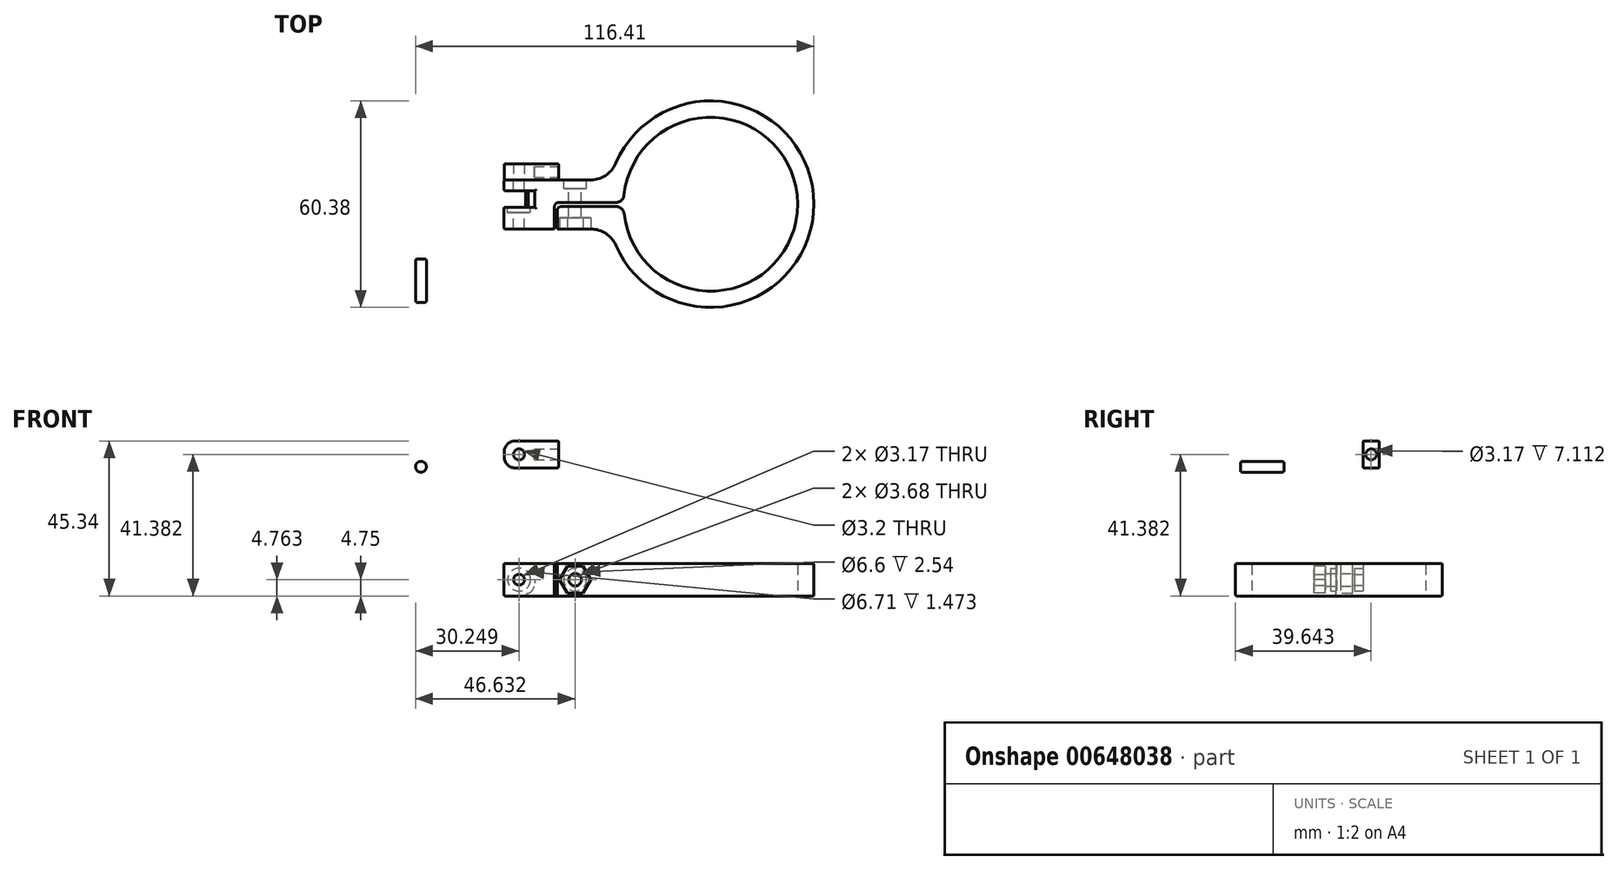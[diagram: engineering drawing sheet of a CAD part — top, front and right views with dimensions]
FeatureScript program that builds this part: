
annotation { "Feature Type Name" : "Feature", "Feature Type Description" : "" }
export const myFeature = defineFeature(function(context is Context, id is Id, definition is map)
    precondition{}
    {
        {
            var Q0;
            Q0=qCreatedBy(makeId("Top.planeOp"),FACE);
            var sketch = newSketch(context, id + "F0", { "sketchPlane" : qUnion([Q0])});
            skLineSegment(sketch, "E0", {"start": v(89.23, 15.92) * mm, "end": v(-89.23, 15.92) * mm, "construction": true});
            skLineSegment(sketch, "E1", {"start": v(-28, 19.91) * mm, "end": v(-19.37, 19.91) * mm});
            skLineSegment(sketch, "E2", {"start": v(-28, 15.1) * mm, "end": v(-19.37, 15.1) * mm});
            skLineSegment(sketch, "E3", {"start": v(-23.98, -123.91) * mm, "end": v(-23.98, 123.91) * mm, "construction": true});
            skLineSegment(sketch, "E4", {"start": v(-28.4, 20.3) * mm, "end": v(-28.4, 22.7) * mm});
            skLineSegment(sketch, "E5", {"start": v(-28.4, 14.7) * mm, "end": v(-28.4, 9.15) * mm});
            skLineSegment(sketch, "E6", {"start": v(-19.37, 15.1) * mm, "end": v(-19.37, 19.91) * mm});
            skArc(sketch, "E7", {"start": v(-28.4, 20.3) * mm, "mid": v(-28.28, 20.03) * mm, "end": v(-28, 19.91) * mm});
            skArc(sketch, "E8", {"start": v(-28, 15.1) * mm, "mid": v(-28.28, 14.98) * mm, "end": v(-28.4, 14.7) * mm});
            skLineSegment(sketch, "E9", {"start": v(-25.57, 13.58) * mm, "end": v(-25.57, 8.75) * mm, "construction": true});
            skLineSegment(sketch, "E10", {"start": v(-22.4, 13.58) * mm, "end": v(-22.4, 8.75) * mm, "construction": true});
            skLineSegment(sketch, "E11", {"start": v(-22.4, 19.91) * mm, "end": v(-22.4, 23.09) * mm, "construction": true});
            skLineSegment(sketch, "E12", {"start": v(-25.57, 19.91) * mm, "end": v(-25.57, 23.09) * mm, "construction": true});
            skLineSegment(sketch, "E13", {"start": v(-28, 23.09) * mm, "end": v(-3.05, 23.09) * mm});
            skLineSegment(sketch, "E14", {"start": v(-25.57, 15.13) * mm, "end": v(-25.57, 19.89) * mm, "construction": true});
            skLineSegment(sketch, "E15", {"start": v(-22.4, 15.13) * mm, "end": v(-22.4, 19.89) * mm, "construction": true});
            skLineSegment(sketch, "E16", {"start": v(-28, 8.75) * mm, "end": v(-14, 8.75) * mm});
            skArc(sketch, "E17", {"start": v(-28.4, 9.15) * mm, "mid": v(-28.28, 8.87) * mm, "end": v(-28, 8.75) * mm});
            skArc(sketch, "E18", {"start": v(-28, 23.09) * mm, "mid": v(-28.28, 22.97) * mm, "end": v(-28.4, 22.7) * mm});
            skLineSegment(sketch, "E19", {"start": v(-13.61, 9.15) * mm, "end": v(-13.61, 15.32) * mm});
            skLineSegment(sketch, "E20", {"start": v(-12.82, 9.15) * mm, "end": v(-12.82, 14.13) * mm});
            skLineSegment(sketch, "E21", {"start": v(-12.42, 8.75) * mm, "end": v(-2.97, 8.75) * mm});
            skLineSegment(sketch, "E22", {"start": v(32, 63.95) * mm, "end": v(32, -37.34) * mm, "construction": true});
            skArc(sketch, "E23", {"start": v(-14, 8.75) * mm, "mid": v(-13.73, 8.87) * mm, "end": v(-13.61, 9.15) * mm});
            skArc(sketch, "E24", {"start": v(-12.82, 9.15) * mm, "mid": v(-12.7, 8.87) * mm, "end": v(-12.42, 8.75) * mm});
            skLineSegment(sketch, "E25", {"start": v(4.34, 16.51) * mm, "end": v(-12.42, 16.51) * mm});
            skLineSegment(sketch, "E26", {"start": v(4.36, 15.32) * mm, "end": v(-11.63, 15.32) * mm});
            skArc(sketch, "E27", {"start": v(-11.63, 15.32) * mm, "mid": v(-12.47, 14.97) * mm, "end": v(-12.82, 14.13) * mm});
            skArc(sketch, "E28", {"start": v(-12.42, 16.51) * mm, "mid": v(-13.26, 16.17) * mm, "end": v(-13.61, 15.32) * mm});
            skLineSegment(sketch, "E29", {"start": v(-27.25, 13.58) * mm, "end": v(-27.25, 15.1) * mm, "construction": true});
            skLineSegment(sketch, "E30", {"start": v(-20.72, 13.58) * mm, "end": v(-20.72, 15.1) * mm, "construction": true});
            skLineSegment(sketch, "E31", {"start": v(-27.25, 13.58) * mm, "end": v(-20.72, 13.58) * mm, "construction": true});
            skArc(sketch, "E32", {"start": v(6.73, 13.2) * mm, "mid": v(57.42, 16.1) * mm, "end": v(6.7, 18.65) * mm});
            skArc(sketch, "E33", {"start": v(4.31, 3.98) * mm, "mid": v(62.18, 16.1) * mm, "end": v(4.25, 27.9) * mm});
            skArc(sketch, "E34", {"start": v(-3.05, 23.09) * mm, "mid": v(1.32, 24.4) * mm, "end": v(4.25, 27.9) * mm});
            skArc(sketch, "E35", {"start": v(4.31, 3.98) * mm, "mid": v(1.38, 7.45) * mm, "end": v(-2.97, 8.75) * mm});
            skArc(sketch, "E36", {"start": v(6.73, 13.2) * mm, "mid": v(5.95, 14.72) * mm, "end": v(4.36, 15.32) * mm});
            skArc(sketch, "E37", {"start": v(4.34, 16.51) * mm, "mid": v(5.93, 17.13) * mm, "end": v(6.7, 18.65) * mm});
            skSolve(sketch);
        }
        {
            var Q0;
            Q0=makeQuery(id+"F0.imprint","IMPRINT",FACE,{"disambiguationData":[TD([[makeQuery(id+"F0.imprint","IMPRINT",EDGE,{"derivedFrom":sQuery(id+"F0.wireOp",EDGE,"E1")}),1.0]])]});
            var Q1;
            Q1=makeQuery(id+"F0.imprint","IMPRINT",FACE,{"disambiguationData":[TD([[makeQuery(id+"F0.imprint","IMPRINT",EDGE,{"derivedFrom":sQuery(id+"F0.wireOp",EDGE,"e81a264f-713f-4254-a722-e31a5868edf8")}),-1.0]])]});
            var Q2;
            Q2 = qSketchRegion(id + "F2", true);
            extrude(context, id + "F1", {"entities" : qUnion([Q0, Q1, Q2]), "depth" : 9.52 * mm, "offsetDistance" : 25.4 * mm});
        }
        {
            var Q0;
            Q0=makeQuery(id+"F1.opExtrude","SWEPT_FACE",FACE,{"disambiguationData":[OSD([sQuery(id+"F0.wireOp",EDGE,"E13")])]});
            var sketch = newSketch(context, id + "F2", { "sketchPlane" : qUnion([Q0])});
            skLineSegment(sketch, "E38", {"start": v(28, 4.76) * mm, "end": v(3.05, 4.76) * mm, "construction": true});
            skLineSegment(sketch, "E39.0", {"start": v(23.98, 100.94) * mm, "end": v(23.98, 0) * mm, "construction": true});
            skCircle(sketch, "E40", {"center": v(23.98, 4.76) * mm, "radius": 1.59 * mm});
            skPoint(sketch, "E41.orphan", {"position": v(23.98, 9.53) * mm});
            skLineSegment(sketch, "E42", {"start": v(5.91, 41.38) * mm, "end": v(51.75, 41.38) * mm, "construction": true});
            skCircle(sketch, "E43", {"center": v(23.98, 41.38) * mm, "radius": 1.6 * mm});
            skLineSegment(sketch, "E44", {"start": v(12.83, 45.34) * mm, "end": v(25.12, 45.34) * mm});
            skLineSegment(sketch, "E45", {"start": v(28.3, 42.17) * mm, "end": v(28.3, 40.6) * mm});
            skLineSegment(sketch, "E46", {"start": v(25.12, 37.42) * mm, "end": v(12.83, 37.42) * mm});
            skLineSegment(sketch, "E47", {"start": v(12.42, 37.83) * mm, "end": v(12.42, 44.94) * mm});
            skPoint(sketch, "E48.visualSharp", {"position": v(28.3, 45.34) * mm});
            skArc(sketch, "E48.filletArc", {"start": v(28.3, 42.17) * mm, "mid": v(27.37, 44.41) * mm, "end": v(25.12, 45.34) * mm});
            skPoint(sketch, "E49.visualSharp", {"position": v(28.3, 37.42) * mm});
            skArc(sketch, "E49.filletArc", {"start": v(25.12, 37.42) * mm, "mid": v(27.37, 38.35) * mm, "end": v(28.3, 40.6) * mm});
            skPoint(sketch, "E50.visualSharp", {"position": v(12.42, 45.34) * mm});
            skArc(sketch, "E50.filletArc", {"start": v(12.83, 45.34) * mm, "mid": v(12.54, 45.23) * mm, "end": v(12.42, 44.94) * mm});
            skPoint(sketch, "E51.visualSharp", {"position": v(12.42, 37.42) * mm});
            skArc(sketch, "E51.filletArc", {"start": v(12.42, 37.83) * mm, "mid": v(12.54, 37.54) * mm, "end": v(12.83, 37.42) * mm});
            skSolve(sketch);
        }
        {
            var Q0;
            Q0=makeQuery(id+"F1.opExtrude","SWEPT_FACE",FACE,{"disambiguationData":[OSD([sQuery(id+"F0.wireOp",EDGE,"E2")])]});
            var sketch = newSketch(context, id + "F3", { "sketchPlane" : qUnion([Q0])});
            skArc(sketch, "E52", {"start": v(19.37, 3.8) * mm, "mid": v(19.9, 1.96) * mm, "end": v(21.34, 0.68) * mm});
            skArc(sketch, "E53", {"start": v(21.34, 0.68) * mm, "mid": v(21.81, 0.48) * mm, "end": v(22.01, 0) * mm});
            skSolve(sketch);
        }
        {
            var Q0;
            {var subQ0=sQuery(id+"F3.wireOp",EDGE,"E52");Q0=makeQuery(id+"F3.imprint","IMPRINT",FACE,{"disambiguationData":[TD([[makeQuery(id+"F3.imprint","IMPRINT",EDGE,{"derivedFrom":subQ0}),-1.0]])]});}
            extrude(context, id + "F4", {"entities" : qUnion([Q0]), "operationType" : NewBodyOperationType.ADD, "depth" : 4.88 * mm, "offsetDistance" : 25.4 * mm, "hasSecondDirection" : true, "secondDirectionOppositeDirection" : false, "secondDirectionDepth" : 0 * mm});
        }
        {
            var Q0;
            Q0=makeQuery(id+"F2.imprint","IMPRINT",FACE,{"disambiguationData":[TD([[makeQuery(id+"F2.imprint","IMPRINT",EDGE,{"derivedFrom":sQuery(id+"F2.wireOp",EDGE,"E40")}),1.0]])]});
            extrude(context, id + "F5", {"entities" : qUnion([Q0]), "operationType" : NewBodyOperationType.REMOVE, "oppositeDirection" : true, "depth" : 16.2 * mm, "offsetDistance" : 25.4 * mm, "hasSecondDirection" : true, "secondDirectionOppositeDirection" : false, "secondDirectionDepth" : 25.4 * mm});
        }
        {
            var Q0;
            Q0=makeQuery(id+"F2.imprint","IMPRINT",FACE,{"disambiguationData":[TD([[makeQuery(id+"F2.imprint","IMPRINT",EDGE,{"derivedFrom":sQuery(id+"F2.wireOp",EDGE,"E40")}),-1.0]])]});
            var sketch = newSketch(context, id + "F6", { "sketchPlane" : qUnion([Q0])});
            skLineSegment(sketch, "E54.0", {"start": v(7.6, 100.94) * mm, "end": v(7.6, 0) * mm, "construction": true});
            skLineSegment(sketch, "E55.0", {"start": v(28, 4.75) * mm, "end": v(3.05, 4.75) * mm, "construction": true});
            skCircle(sketch, "E56", {"center": v(7.6, 4.75) * mm, "radius": 1.84 * mm});
            skCircle(sketch, "E57", {"center": v(7.6, 4.75) * mm, "radius": 3.3 * mm});
            skSolve(sketch);
        }
        {
            var Q0;
            Q0=makeQuery(id+"F1.opExtrude","SWEPT_FACE",FACE,{"disambiguationData":[OSD([sQuery(id+"F0.wireOp",EDGE,"E21")])]});
            var sketch = newSketch(context, id + "F7", { "sketchPlane" : qUnion([Q0])});
            skPoint(sketch, "E58.0.midPoint", {"position": v(-7.6, 0.75) * mm});
            skPoint(sketch, "E59.0.midPoint", {"position": v(-7.6, 0.85) * mm});
            skLineSegment(sketch, "E60.0", {"start": v(-12.42, 4.75) * mm, "end": v(-2.97, 4.75) * mm, "construction": true});
            skLineSegment(sketch, "E61.0", {"start": v(-7.6, 100.94) * mm, "end": v(-7.6, 0) * mm, "construction": true});
            skLineSegment(sketch, "E62.0", {"start": v(-5.34, 0.8) * mm, "end": v(-9.88, 0.82) * mm});
            skLineSegment(sketch, "E62.1", {"start": v(-9.88, 0.82) * mm, "end": v(-12.14, 4.76) * mm});
            skLineSegment(sketch, "E62.2", {"start": v(-12.14, 4.76) * mm, "end": v(-9.86, 8.7) * mm});
            skLineSegment(sketch, "E62.3", {"start": v(-9.86, 8.7) * mm, "end": v(-5.31, 8.68) * mm});
            skLineSegment(sketch, "E62.4", {"start": v(-5.31, 8.68) * mm, "end": v(-3.05, 4.74) * mm});
            skLineSegment(sketch, "E62.5", {"start": v(-3.05, 4.74) * mm, "end": v(-5.34, 0.8) * mm});
            skPoint(sketch, "E62.0.midPoint", {"position": v(-7.6, 0.81) * mm});
            skSolve(sketch);
        }
        {
            var Q0;
            Q0=makeQuery(id+"F1.opExtrude","CAP_EDGE",EDGE,{"disambiguationData":[OSD([sQuery(id+"F0.wireOp",EDGE,"E35")])],"isStart":true});
            var Q1;
            Q1=makeQuery(id+"F1.opExtrude","CAP_EDGE",EDGE,{"disambiguationData":[OSD([sQuery(id+"F0.wireOp",EDGE,"E35")])],"isStart":false});
            var Q2;
            Q2=makeQuery(id+"F1.opExtrude","CAP_EDGE",EDGE,{"disambiguationData":[OSD([sQuery(id+"F0.wireOp",EDGE,"E6")])],"isStart":false});
            fillet(context, id + "F8", {"entities" : qUnion([Q0, Q1, Q2]), "radius" : 0.38 * mm, "tangentPropagation" : true, "allowEdgeOverflow" : false});
        }
        {
            var Q0;
            Q0=makeQuery(id+"F2.imprint","IMPRINT",FACE,{"disambiguationData":[TD([[makeQuery(id+"F2.imprint","IMPRINT",EDGE,{"derivedFrom":sQuery(id+"F2.wireOp",EDGE,"E43")}),-1.0]])]});
            extrude(context, id + "F9", {"entities" : qUnion([Q0]), "depth" : 4.75 * mm, "offsetDistance" : 25.4 * mm});
        }
        {
            var Q0;
            Q0=makeQuery(id+"F9.opExtrude","CAP_EDGE",EDGE,{"disambiguationData":[OSD([sQuery(id+"F2.wireOp",EDGE,"E46")])],"isStart":false});
            var Q1;
            Q1=makeQuery(id+"F9.opExtrude","CAP_EDGE",EDGE,{"disambiguationData":[OSD([sQuery(id+"F2.wireOp",EDGE,"E46")])],"isStart":true});
            var Q2;
            Q2=makeQuery(id+"F9.opExtrude","SWEPT_FACE",FACE,{"disambiguationData":[OSD([sQuery(id+"F2.wireOp",EDGE,"E47")])]});
            fillet(context, id + "F10", {"entities" : qUnion([Q0, Q1, Q2]), "radius" : 0.38 * mm, "tangentPropagation" : true, "allowEdgeOverflow" : false});
        }
        {
            var Q0;
            Q0=makeQuery(id+"F9.opExtrude","SWEPT_FACE",FACE,{"disambiguationData":[OSD([sQuery(id+"F2.wireOp",EDGE,"E47")])]});
            var sketch = newSketch(context, id + "F11", { "sketchPlane" : qUnion([Q0])});
            skLineSegment(sketch, "E63", {"start": v(25.46, 44.94) * mm, "end": v(25.46, 37.83) * mm, "construction": true});
            skLineSegment(sketch, "E64", {"start": v(27.46, 41.38) * mm, "end": v(23.47, 41.38) * mm, "construction": true});
            skCircle(sketch, "E65", {"center": v(25.46, 41.38) * mm, "radius": 1.59 * mm});
            skSolve(sketch);
        }
        {
            var Q0;
            Q0=makeQuery(id+"F11.imprint","IMPRINT",FACE,{"disambiguationData":[TD([[makeQuery(id+"F11.imprint","IMPRINT",EDGE,{"derivedFrom":sQuery(id+"F11.wireOp",EDGE,"E65")}),1.0]])]});
            extrude(context, id + "F12", {"entities" : qUnion([Q0]), "operationType" : NewBodyOperationType.REMOVE, "oppositeDirection" : true, "depth" : 7.11 * mm, "offsetDistance" : 25.4 * mm});
        }
        {
            var Q0;
            Q0=qCreatedBy(makeId("Front.planeOp"),FACE);
            var sketch = newSketch(context, id + "F13", { "sketchPlane" : qUnion([Q0])});
            skCircle(sketch, "E66", {"center": v(-52.64, 37.76) * mm, "radius": 1.59 * mm});
            skSolve(sketch);
        }
        {
            var Q0;
            Q0=makeQuery(id+"F13.imprint","IMPRINT",FACE,{"disambiguationData":[TD([[makeQuery(id+"F13.imprint","IMPRINT",EDGE,{"derivedFrom":sQuery(id+"F13.wireOp",EDGE,"E66")}),1.0]])]});
            extrude(context, id + "F14", {"entities" : qUnion([Q0]), "depth" : 12.7 * mm, "offsetDistance" : 25.4 * mm});
        }
        {
            var Q0;
            Q0=makeQuery(id+"F14.opExtrude","CAP_EDGE",EDGE,{"disambiguationData":[OSD([sQuery(id+"F13.wireOp",EDGE,"E66")])],"isStart":true});
            var Q1;
            Q1=makeQuery(id+"F14.opExtrude","CAP_EDGE",EDGE,{"disambiguationData":[OSD([sQuery(id+"F13.wireOp",EDGE,"E66")])],"isStart":false});
            fillet(context, id + "F15", {"entities" : qUnion([Q0, Q1]), "radius" : 0.5 * mm, "tangentPropagation" : true, "allowEdgeOverflow" : false});
        }
        {
            var Q0;
            Q0=makeQuery(id+"F6.imprint","IMPRINT",FACE,{"disambiguationData":[TD([[makeQuery(id+"F6.imprint","IMPRINT",EDGE,{"derivedFrom":sQuery(id+"F6.wireOp",EDGE,"E56")}),1.0]])]});
            extrude(context, id + "F16", {"entities" : qUnion([Q0]), "operationType" : NewBodyOperationType.REMOVE, "oppositeDirection" : true, "depth" : 25.4 * mm, "offsetDistance" : 25.4 * mm});
        }
        {
            var Q0;
            Q0=makeQuery(id+"F6.imprint","IMPRINT",FACE,{"disambiguationData":[TD([[makeQuery(id+"F6.imprint","IMPRINT",EDGE,{"derivedFrom":sQuery(id+"F6.wireOp",EDGE,"E56")}),-1.0]])]});
            extrude(context, id + "F17", {"entities" : qUnion([Q0]), "operationType" : NewBodyOperationType.REMOVE, "oppositeDirection" : true, "depth" : 2.54 * mm, "offsetDistance" : 25.4 * mm});
        }
        {
            var Q0;
            Q0=makeQuery(id+"F7.imprint","IMPRINT",FACE,{"disambiguationData":[TD([[makeQuery(id+"F7.imprint","IMPRINT",EDGE,{"derivedFrom":sQuery(id+"F7.wireOp",EDGE,"E62.0")}),-1.0]])]});
            extrude(context, id + "F18", {"entities" : qUnion([Q0]), "operationType" : NewBodyOperationType.REMOVE, "oppositeDirection" : true, "depth" : 3.3 * mm, "offsetDistance" : 25.4 * mm});
        }
        {
            var Q0;
            {var subQ4=sQuery(id+"F3.wireOp",EDGE,"E52");Q0=makeQuery(id+"F3.imprint","IMPRINT",FACE,{"disambiguationData":[TD([[makeQuery(id+"F3.imprint","IMPRINT",EDGE,{"derivedFrom":subQ4}),1.0]])]});}
            var sketch = newSketch(context, id + "F19", { "sketchPlane" : qUnion([Q0])});
            skCircle(sketch, "E67.0", {"center": v(23.98, 4.76) * mm, "radius": 1.59 * mm});
            skCircle(sketch, "E68", {"center": v(23.98, 4.76) * mm, "radius": 3.35 * mm});
            skSolve(sketch);
        }
        {
            var Q0;
            Q0=makeQuery(id+"F19.imprint","IMPRINT",FACE,{"disambiguationData":[TD([[makeQuery(id+"F19.imprint","IMPRINT",EDGE,{"derivedFrom":sQuery(id+"F19.wireOp",EDGE,"E67.0")}),-1.0]])]});
            extrude(context, id + "F20", {"entities" : qUnion([Q0]), "operationType" : NewBodyOperationType.REMOVE, "oppositeDirection" : true, "depth" : 1.47 * mm, "offsetDistance" : 25.4 * mm});
        }
    });
